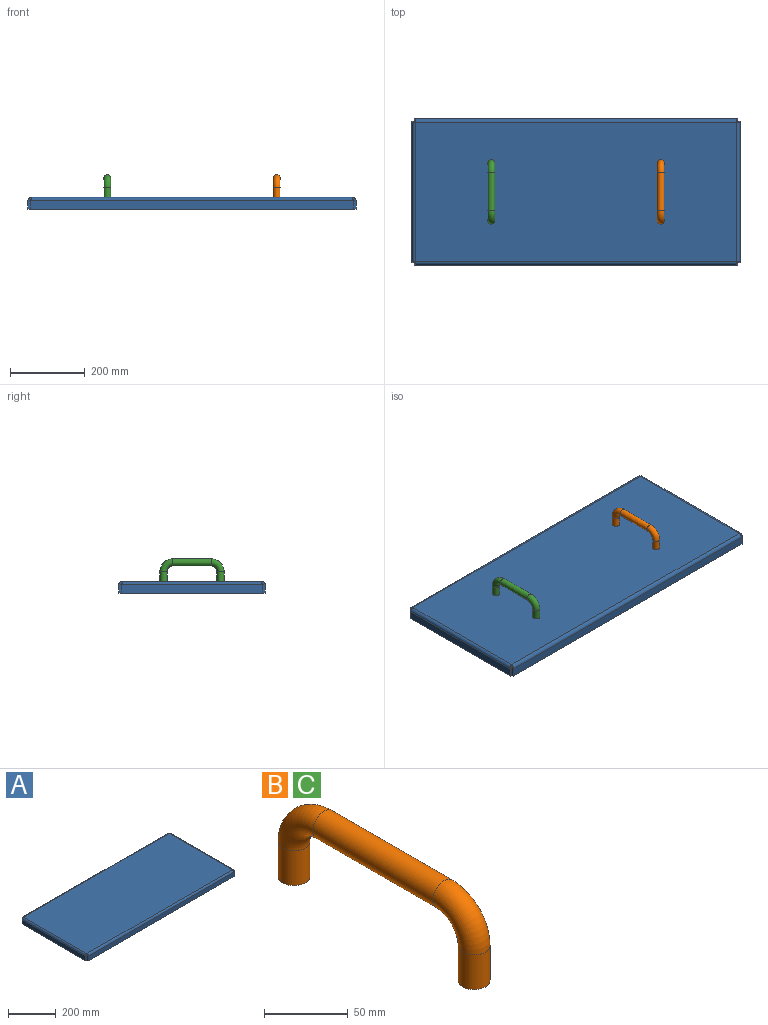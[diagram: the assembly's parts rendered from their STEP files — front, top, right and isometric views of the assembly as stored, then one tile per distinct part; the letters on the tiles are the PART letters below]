
ASSEMBLY  parts=3 mates=1
PART A: 46 faces, bbox 876.3x390.5x31.8 mm
  f0: plane 6.35x2.26mm, normal (0,0,1), area 14.4mm2, adj f4,f5,f6,f43
  f1: plane 6.35x2.26mm, normal (0,0,1), area 14.4mm2, adj f2,f5,f6,f42
  f2: plane 23.11x6.35mm, normal (1,0,0), area 146.8mm2, adj f1,f3,f5,f6
  f3: plane 863.55x6.35mm, normal (0,0,-1), area 5483.5mm2, adj f2,f4,f5,f6
  f4: plane 23.11x6.35mm, normal (-1,0,0), area 146.8mm2, adj f0,f3,f5,f6
  f5: plane 863.55x23.11mm, normal (0,1,0), area 19960.1mm2, adj f0,f1,f2,f3,f4,f44
  f6: plane 863.55x23.11mm, normal (0,-1,0), area 19960.1mm2, adj f0,f1,f2,f3,f4,f45
  f7: plane 859.03x373.25mm, normal (0,0,1), area 320634.8mm2, adj f18,f29,f40,f44
  f8: plane 859.03x373.25mm, normal (0,0,-1), area 320634.8mm2, adj f19,f30,f41,f45
  f9: plane 6.35x2.26mm, normal (0,0,1), area 14.4mm2, adj f13,f14,f15,f17
  f10: plane 6.35x2.26mm, normal (0,0,1), area 14.4mm2, adj f11,f14,f15,f16
  f11: plane 23.11x6.35mm, normal (0,1,0), area 146.8mm2, adj f10,f12,f14,f15
  f12: plane 377.77x6.35mm, normal (0,0,-1), area 2398.9mm2, adj f11,f13,f14,f15
  f13: plane 23.11x6.35mm, normal (0,-1,0), area 146.8mm2, adj f9,f12,f14,f15
  f14: plane 377.77x23.11mm, normal (-1,0,0), area 8731.9mm2, adj f9,f10,f11,f12,f13,f18
  f15: plane 377.77x23.11mm, normal (1,0,0), area 8731.9mm2, adj f9,f10,f11,f12,f13,f19
  f16: plane 8.64x8.64mm, normal (0,1,0), area 54.5mm2, adj f10,f18,f19,f43
  f17: plane 8.64x8.64mm, normal (0,-1,0), area 54.5mm2, adj f9,f18,f19,f27
  f18: cylinder r=8.64mm len=373.25mm, axis (0,1,0), area 5063.3mm2, adj f7,f14,f16,f17
  f19: cylinder r=2.29mm len=373.25mm, axis (0,1,0), area 1340.3mm2, adj f8,f15,f16,f17
  f20: plane 6.35x2.26mm, normal (0,0,1), area 14.4mm2, adj f24,f25,f26,f28
  f21: plane 6.35x2.26mm, normal (0,0,1), area 14.4mm2, adj f22,f25,f26,f27
  f22: plane 23.11x6.35mm, normal (-1,0,0), area 146.8mm2, adj f21,f23,f25,f26
  f23: plane 863.55x6.35mm, normal (0,0,-1), area 5483.5mm2, adj f22,f24,f25,f26
  f24: plane 23.11x6.35mm, normal (1,0,0), area 146.8mm2, adj f20,f23,f25,f26
  f25: plane 863.55x23.11mm, normal (0,-1,0), area 19960.1mm2, adj f20,f21,f22,f23,f24,f29
  f26: plane 863.55x23.11mm, normal (0,1,0), area 19960.1mm2, adj f20,f21,f22,f23,f24,f30
  f27: plane 8.64x8.64mm, normal (-1,0,0), area 54.5mm2, adj f17,f21,f29,f30
  f28: plane 8.64x8.64mm, normal (1,0,0), area 54.5mm2, adj f20,f29,f30,f38
  f29: cylinder r=8.64mm len=859.03mm, axis (-1,0,0), area 11653.1mm2, adj f7,f25,f27,f28
  f30: cylinder r=2.29mm len=859.03mm, axis (-1,0,0), area 3084.6mm2, adj f8,f26,f27,f28
  f31: plane 6.35x2.26mm, normal (0,0,1), area 14.4mm2, adj f35,f36,f37,f39
  f32: plane 6.35x2.26mm, normal (0,0,1), area 14.4mm2, adj f33,f36,f37,f38
  f33: plane 23.11x6.35mm, normal (0,-1,0), area 146.8mm2, adj f32,f34,f36,f37
  f34: plane 377.77x6.35mm, normal (0,0,-1), area 2398.9mm2, adj f33,f35,f36,f37
  f35: plane 23.11x6.35mm, normal (0,1,0), area 146.8mm2, adj f31,f34,f36,f37
  f36: plane 377.77x23.11mm, normal (1,0,0), area 8731.9mm2, adj f31,f32,f33,f34,f35,f40
  f37: plane 377.77x23.11mm, normal (-1,0,0), area 8731.9mm2, adj f31,f32,f33,f34,f35,f41
  f38: plane 8.64x8.64mm, normal (0,-1,0), area 54.5mm2, adj f28,f32,f40,f41
  f39: plane 8.64x8.64mm, normal (0,1,0), area 54.5mm2, adj f31,f40,f41,f42
  f40: cylinder r=8.64mm len=373.25mm, axis (0,-1,0), area 5063.3mm2, adj f7,f36,f38,f39
  f41: cylinder r=2.29mm len=373.25mm, axis (0,-1,0), area 1340.3mm2, adj f8,f37,f38,f39
  f42: plane 8.64x8.64mm, normal (1,0,0), area 54.5mm2, adj f1,f39,f44,f45
  f43: plane 8.64x8.64mm, normal (-1,0,0), area 54.5mm2, adj f0,f16,f44,f45
  f44: cylinder r=8.64mm len=859.03mm, axis (1,0,0), area 11653.1mm2, adj f5,f7,f42,f43
  f45: cylinder r=2.29mm len=859.03mm, axis (1,0,0), area 3084.6mm2, adj f6,f8,f42,f43
PART B: 7 faces, bbox 19.1x177.2x63.2 mm
  f0: plane 19.05x19.05mm, normal (0,0,-1), area 285mm2, adj f2
  f1: plane 19.05x19.05mm, normal (0,0,-1), area 285mm2, adj f6
  f2: cylinder r=9.53mm len=25.4mm, axis (0,0,1), area 1520.1mm2, adj f0,f3
  f3: torus R=25.4mm, axis (-1,0,0), area 2387.8mm2, adj f2,f4
  f4: cylinder r=9.53mm len=101.6mm, axis (0,1,0), area 6080.5mm2, adj f3,f5
  f5: torus R=25.4mm, axis (-1,0,0), area 2387.8mm2, adj f4,f6
  f6: cylinder r=9.53mm len=25.4mm, axis (0,0,-1), area 1520.1mm2, adj f1,f5
PART C: same geometry as B
PLACE A at identity
PLACE B rot(axis=(0,0,1),180deg) t=(0,-485.77,0)mm
PLACE C at identity
MATE fastened C.f2 <-> A.f7  axis (0,0,-1) through (-226.31,-319.09,308.49)mm
